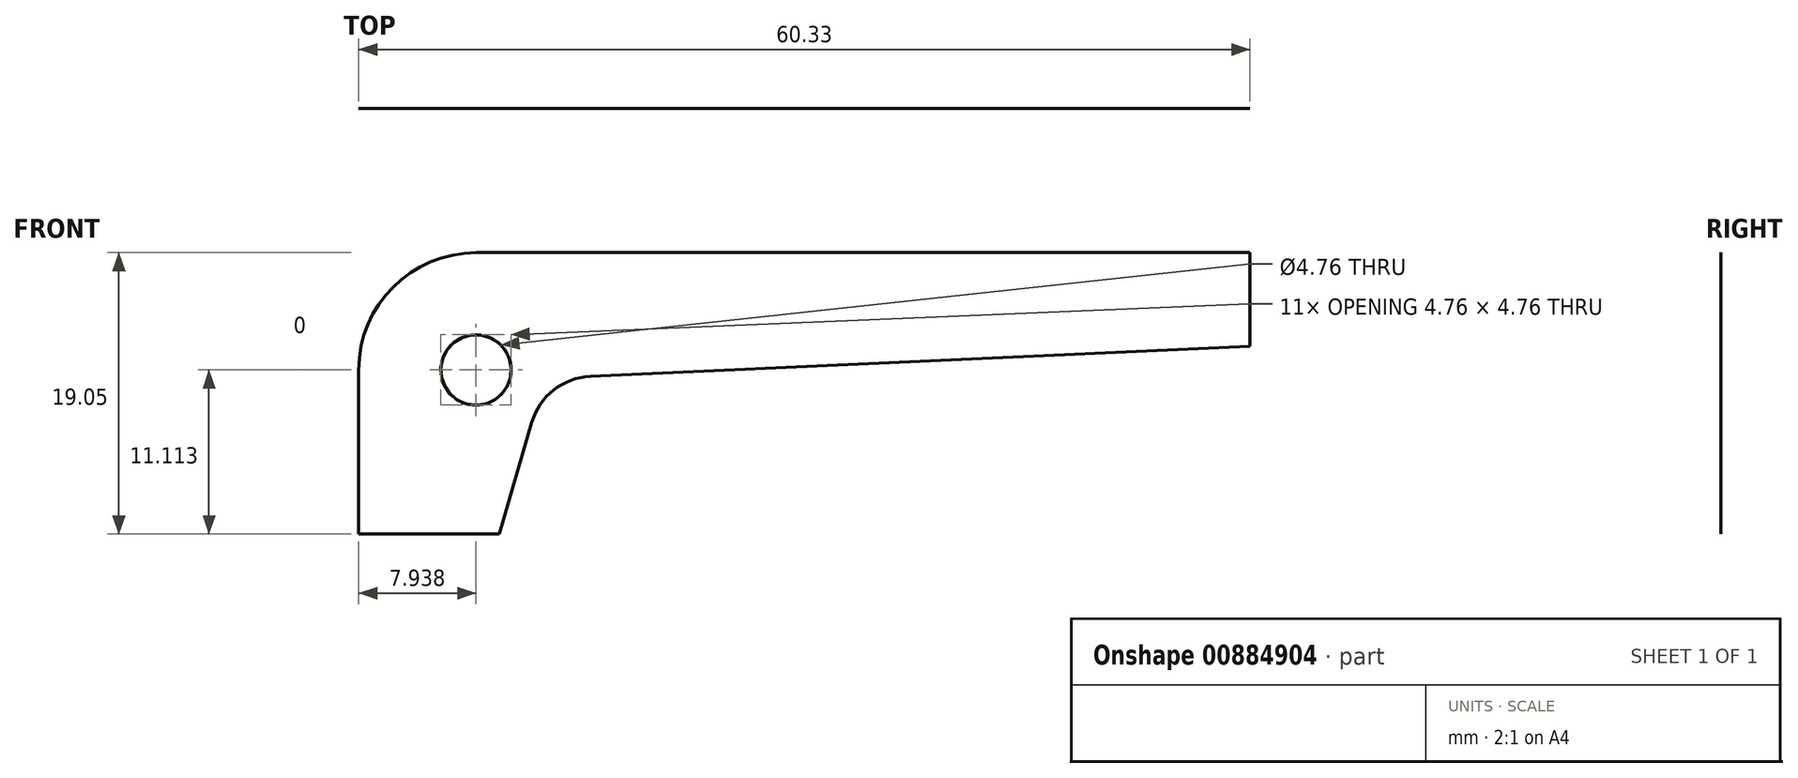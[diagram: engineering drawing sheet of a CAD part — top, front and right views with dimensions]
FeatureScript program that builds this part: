
annotation { "Feature Type Name" : "Feature", "Feature Type Description" : "" }
export const myFeature = defineFeature(function(context is Context, id is Id, definition is map)
    precondition{}
    {
        {
            var Q0;
            Q0=qCreatedBy(makeId("Front.planeOp"),FACE);
            var sketch = newSketch(context, id + "F0", { "sketchPlane" : qUnion([Q0])});
            skLineSegment(sketch, "E0.top", {"start": v(7.95, 19.05) * mm, "end": v(60.33, 19.05) * mm});
            skLineSegment(sketch, "E0.left", {"start": v(0, 0) * mm, "end": v(0, 11.1) * mm});
            skLineSegment(sketch, "E1", {"start": v(9.53, 0) * mm, "end": v(11.72, 7.56) * mm});
            skLineSegment(sketch, "E2", {"start": v(60.33, 12.7) * mm, "end": v(15.68, 10.68) * mm});
            skLineSegment(sketch, "E3", {"start": v(60.33, 19.05) * mm, "end": v(60.33, 12.7) * mm});
            skLineSegment(sketch, "E4", {"start": v(0, 0) * mm, "end": v(9.53, 0) * mm});
            skArc(sketch, "E5", {"start": v(15.68, 10.68) * mm, "mid": v(13.2, 9.75) * mm, "end": v(11.72, 7.56) * mm});
            skPoint(sketch, "E6.visualSharp", {"position": v(0, 19.05) * mm});
            skArc(sketch, "E6.filletArc", {"start": v(7.95, 19.05) * mm, "mid": v(2.33, 16.72) * mm, "end": v(0, 11.1) * mm});
            skSolve(sketch);
        }
        {
            var Q0;
            Q0=makeQuery(id+"F0.imprint","IMPRINT",FACE,{"disambiguationData":[TD([[makeQuery(id+"F0.imprint","IMPRINT",EDGE,{"derivedFrom":sQuery(id+"F0.wireOp",EDGE,"E0.top")}),-1.0]])]});
            extrude(context, id + "F1", {"entities" : qUnion([Q0]), "depth" : 3 / 812.8 * mm, "offsetDistance" : 25.4 * mm});
        }
        {
            var Q0;
            Q0=makeQuery(id+"F1.opExtrude","CAP_FACE",FACE,{"disambiguationData":[OSD([sQuery(id+"F0.wireOp",EDGE,"E0.top"),sQuery(id+"F0.wireOp",EDGE,"E0.left"),sQuery(id+"F0.wireOp",EDGE,"E1"),sQuery(id+"F0.wireOp",EDGE,"E2"),sQuery(id+"F0.wireOp",EDGE,"E3"),sQuery(id+"F0.wireOp",EDGE,"E4"),sQuery(id+"F0.wireOp",EDGE,"E5"),sQuery(id+"F0.wireOp",EDGE,"E6.filletArc")])],"isStart":false});
            var sketch = newSketch(context, id + "F2", { "sketchPlane" : qUnion([Q0])});
            skCircle(sketch, "E7", {"center": v(7.94, 11.11) * mm, "radius": 2.38 * mm});
            skSolve(sketch);
        }
        {
            var Q0;
            Q0=makeQuery(id+"F2.imprint","IMPRINT",FACE,{"disambiguationData":[TD([[makeQuery(id+"F2.imprint","IMPRINT",EDGE,{"derivedFrom":sQuery(id+"F2.wireOp",EDGE,"E7")}),1.0]])]});
            extrude(context, id + "F3", {"entities" : qUnion([Q0]), "operationType" : NewBodyOperationType.REMOVE, "oppositeDirection" : true, "depth" : 25.4 * mm, "offsetDistance" : 25.4 * mm});
        }
        {
            var Q0;
            Q0=makeQuery(id+"F1.opExtrude","SWEPT_FACE",FACE,{"disambiguationData":[OSD([sQuery(id+"F0.wireOp",EDGE,"E0.top")])]});
            var sketch = newSketch(context, id + "F4", { "sketchPlane" : qUnion([Q0])});
            skLineSegment(sketch, "E8", {"start": v(45.24, 0) * mm, "end": v(60.33, -0.8) * mm});
            skLineSegment(sketch, "E9", {"start": v(60.33, -0.8) * mm, "end": v(60.33, 0) * mm});
            skLineSegment(sketch, "E10", {"start": v(60.33, 0) * mm, "end": v(45.24, 0) * mm});
            skLineSegment(sketch, "E11.MirrorCS", {"start": v(45.24, -2.38) * mm, "end": v(60.33, -1.59) * mm});
            skLineSegment(sketch, "E12.MirrorCS", {"start": v(60.33, -2.38) * mm, "end": v(45.24, -2.38) * mm});
            skLineSegment(sketch, "E13.MirrorCS", {"start": v(60.33, -1.59) * mm, "end": v(60.33, -2.38) * mm});
            skSolve(sketch);
        }
        {
            var Q0;
            Q0=makeQuery(id+"F4.imprint","IMPRINT",FACE,{"disambiguationData":[TD([[makeQuery(id+"F4.imprint","IMPRINT",EDGE,{"derivedFrom":sQuery(id+"F4.wireOp",EDGE,"E8")}),1.0]])]});
            var Q1;
            Q1=makeQuery(id+"F4.imprint","IMPRINT",FACE,{"disambiguationData":[TD([[makeQuery(id+"F4.imprint","IMPRINT",EDGE,{"derivedFrom":sQuery(id+"F4.wireOp",EDGE,"E11.MirrorCS")}),-1.0]])]});
            extrude(context, id + "F5", {"entities" : qUnion([Q0, Q1]), "operationType" : NewBodyOperationType.REMOVE, "oppositeDirection" : true, "depth" : 25.4 * mm, "offsetDistance" : 25.4 * mm});
        }
    });
